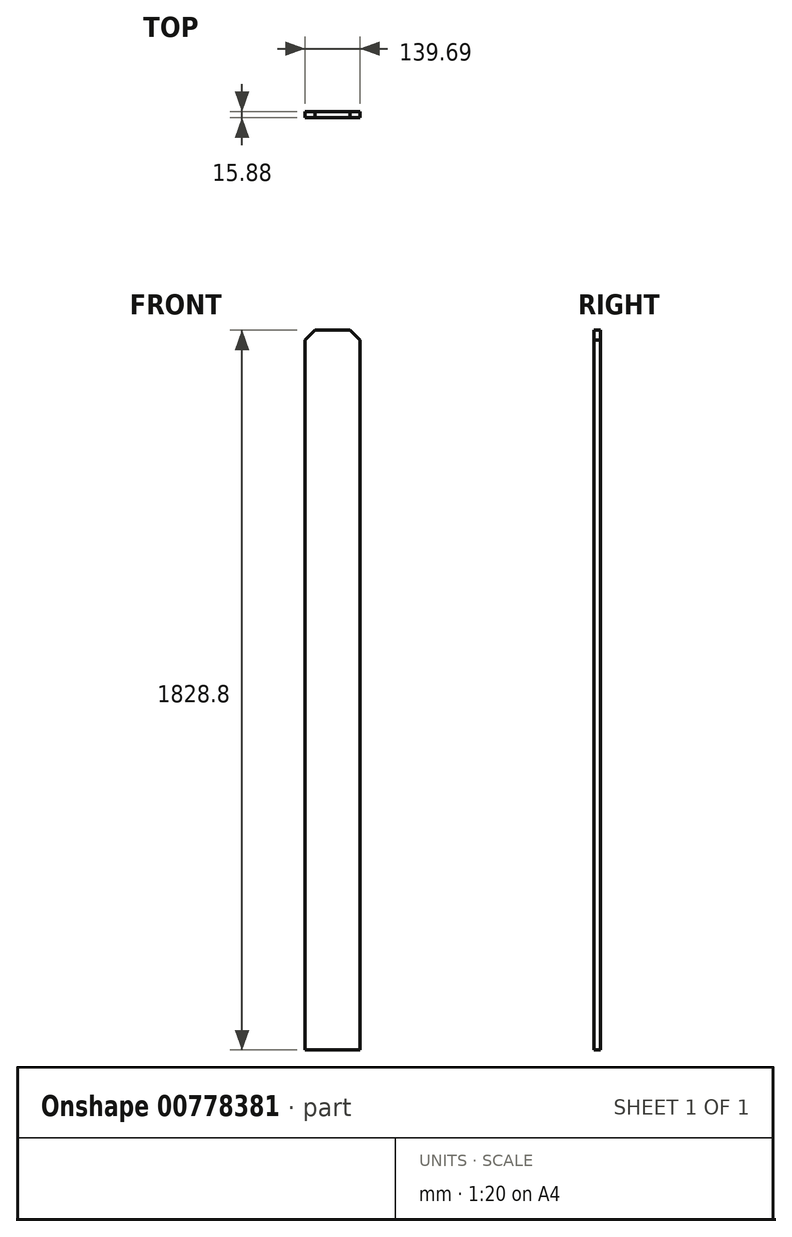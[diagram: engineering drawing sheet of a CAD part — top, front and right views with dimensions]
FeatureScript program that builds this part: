
annotation { "Feature Type Name" : "Feature", "Feature Type Description" : "" }
export const myFeature = defineFeature(function(context is Context, id is Id, definition is map)
    precondition{}
    {
        {
            var Q0;
            Q0=qCreatedBy(makeId("Front.planeOp"),FACE);
            var sketch = newSketch(context, id + "F0", { "sketchPlane" : qUnion([Q0])});
            skLineSegment(sketch, "E0", {"start": v(0, 0) * mm, "end": v(0, 1803.4) * mm});
            skLineSegment(sketch, "E1", {"start": v(0, 1803.4) * mm, "end": v(25.4, 1828.8) * mm});
            skLineSegment(sketch, "E2", {"start": v(25.4, 1828.8) * mm, "end": v(114.3, 1828.8) * mm});
            skLineSegment(sketch, "E3", {"start": v(114.3, 1828.8) * mm, "end": v(139.7, 1803.4) * mm});
            skLineSegment(sketch, "E4", {"start": v(139.7, 1803.4) * mm, "end": v(139.7, 0) * mm});
            skLineSegment(sketch, "E5", {"start": v(0, 0) * mm, "end": v(139.7, 0) * mm});
            skSolve(sketch);
        }
        {
            var Q0;
            Q0 = qSketchRegion(id + "F0", true);
            extrude(context, id + "F1", {"entities" : qUnion([Q0]), "depth" : 15.88 * mm, "offsetDistance" : 25.4 * mm});
        }
    });
